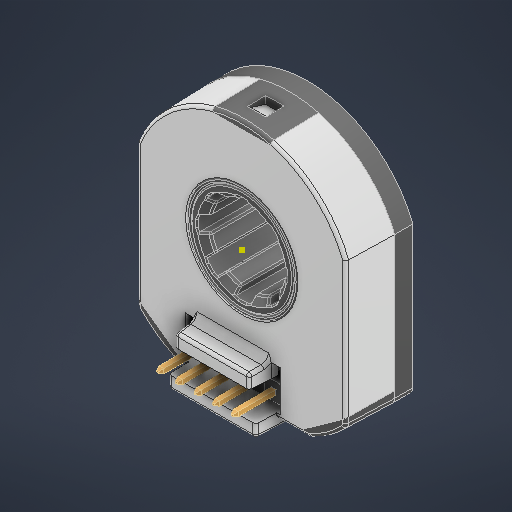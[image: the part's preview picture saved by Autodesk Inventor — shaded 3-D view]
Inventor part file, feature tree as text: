
AUTODESK INVENTOR PART (.ipt)
format: ipt  version: 2025 (Build 290162000, 162)  size: 1,170,432 bytes
history: native  units: mm
features: sketch x1
ambient origin geometry x8: Origin, YZ Plane, XZ Plane, XY Plane, X Axis, Y Axis, Z Axis, Center Point
bodies: Solid1 (feature_tree), Solid2 (feature_tree), Solid3 (feature_tree), Solid6 (feature_tree), Solid7 (feature_tree), Solid8 (feature_tree), Solid9 (feature_tree), Solid10 (feature_tree), Solid11 (feature_tree), Solid12 (feature_tree), Solid13 (feature_tree), Solid14 (feature_tree), Solid15 (feature_tree)
feature tree (1):
  sketch  "Sketch1"
